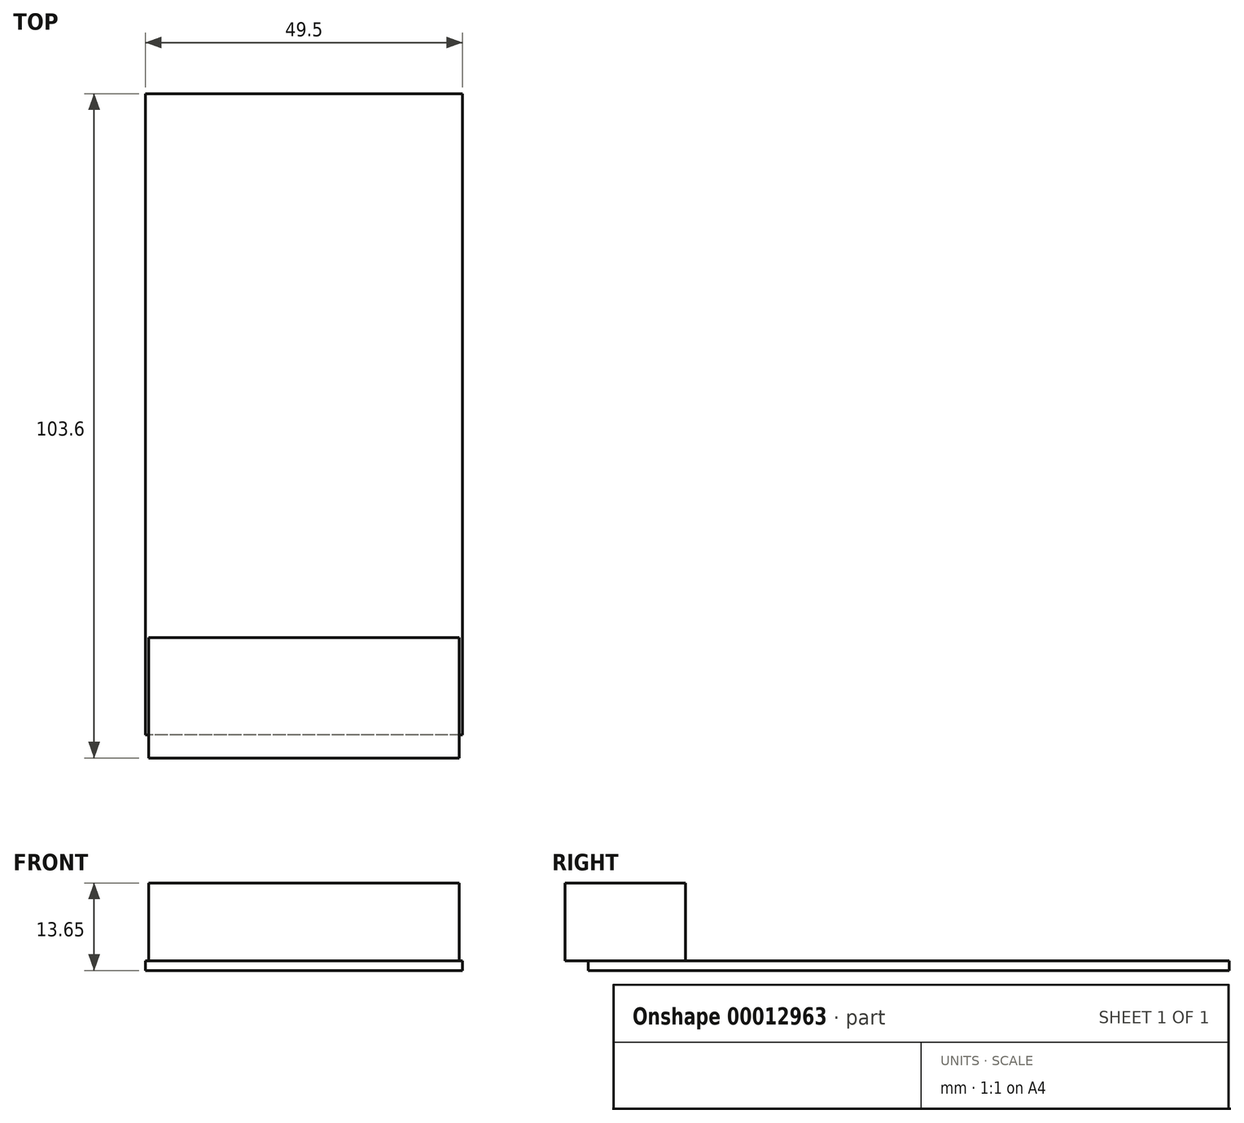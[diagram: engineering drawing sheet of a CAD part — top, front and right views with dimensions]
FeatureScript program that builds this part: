
annotation { "Feature Type Name" : "Feature", "Feature Type Description" : "" }
export const myFeature = defineFeature(function(context is Context, id is Id, definition is map)
    precondition{}
    {
        {
            var Q0;
            Q0=qCreatedBy(makeId("Top.planeOp"),FACE);
            var sketch = newSketch(context, id + "F0", { "sketchPlane" : qUnion([Q0])});
            skLineSegment(sketch, "E0.rect.bottom", {"start": v(24.75, 50) * mm, "end": v(-24.75, 50) * mm});
            skLineSegment(sketch, "E0.rect.top", {"start": v(24.75, -50) * mm, "end": v(-24.75, -50) * mm});
            skLineSegment(sketch, "E0.rect.left", {"start": v(24.75, 50) * mm, "end": v(24.75, -50) * mm});
            skLineSegment(sketch, "E0.rect.right", {"start": v(-24.75, 50) * mm, "end": v(-24.75, -50) * mm});
            skPoint(sketch, "E0.rect.middle", {"position": v(0, 0) * mm});
            skSolve(sketch);
        }
        {
            var Q0;
            Q0=makeQuery(id+"F0.imprint","IMPRINT",FACE,{"disambiguationData":[TD([[makeQuery(id+"F0.imprint","IMPRINT",EDGE,{"derivedFrom":sQuery(id+"F0.wireOp",EDGE,"E0.rect.bottom")}),1.0]])]});
            extrude(context, id + "F1", {"entities" : qUnion([Q0]), "depth" : 1.5 * mm});
        }
        {
            var Q0;
            Q0=makeQuery(id+"F1.opExtrude","CAP_FACE",FACE,{"disambiguationData":[OSD([sQuery(id+"F0.wireOp",EDGE,"E0.rect.bottom"),sQuery(id+"F0.wireOp",EDGE,"E0.rect.top"),sQuery(id+"F0.wireOp",EDGE,"E0.rect.left"),sQuery(id+"F0.wireOp",EDGE,"E0.rect.right")])],"isStart":false});
            var sketch = newSketch(context, id + "F2", { "sketchPlane" : qUnion([Q0])});
            skLineSegment(sketch, "E1.bottom", {"start": v(-24.25, -34.85) * mm, "end": v(24.25, -34.85) * mm});
            skLineSegment(sketch, "E1.top", {"start": v(-24.25, -53.6) * mm, "end": v(24.25, -53.6) * mm});
            skLineSegment(sketch, "E1.left", {"start": v(-24.25, -34.85) * mm, "end": v(-24.25, -53.6) * mm});
            skLineSegment(sketch, "E1.right", {"start": v(24.25, -34.85) * mm, "end": v(24.25, -53.6) * mm});
            skSolve(sketch);
        }
        {
            var Q0;
            {var subQ5=sQuery(id+"F2.wireOp",EDGE,"E1.bottom");Q0=makeQuery(id+"F2.imprint","IMPRINT",FACE,{"disambiguationData":[TD([[makeQuery(id+"F2.imprint","IMPRINT",EDGE,{"derivedFrom":subQ5}),-1.0]])]});}
            var Q1;
            {var subQ5=sQuery(id+"F2.wireOp",EDGE,"E1.top");Q1=makeQuery(id+"F2.imprint","IMPRINT",FACE,{"disambiguationData":[TD([[makeQuery(id+"F2.imprint","IMPRINT",EDGE,{"derivedFrom":subQ5}),1.0]])]});}
            extrude(context, id + "F3", {"entities" : qUnion([Q0, Q1]), "operationType" : NewBodyOperationType.ADD, "depth" : 12.15 * mm});
        }
    });
